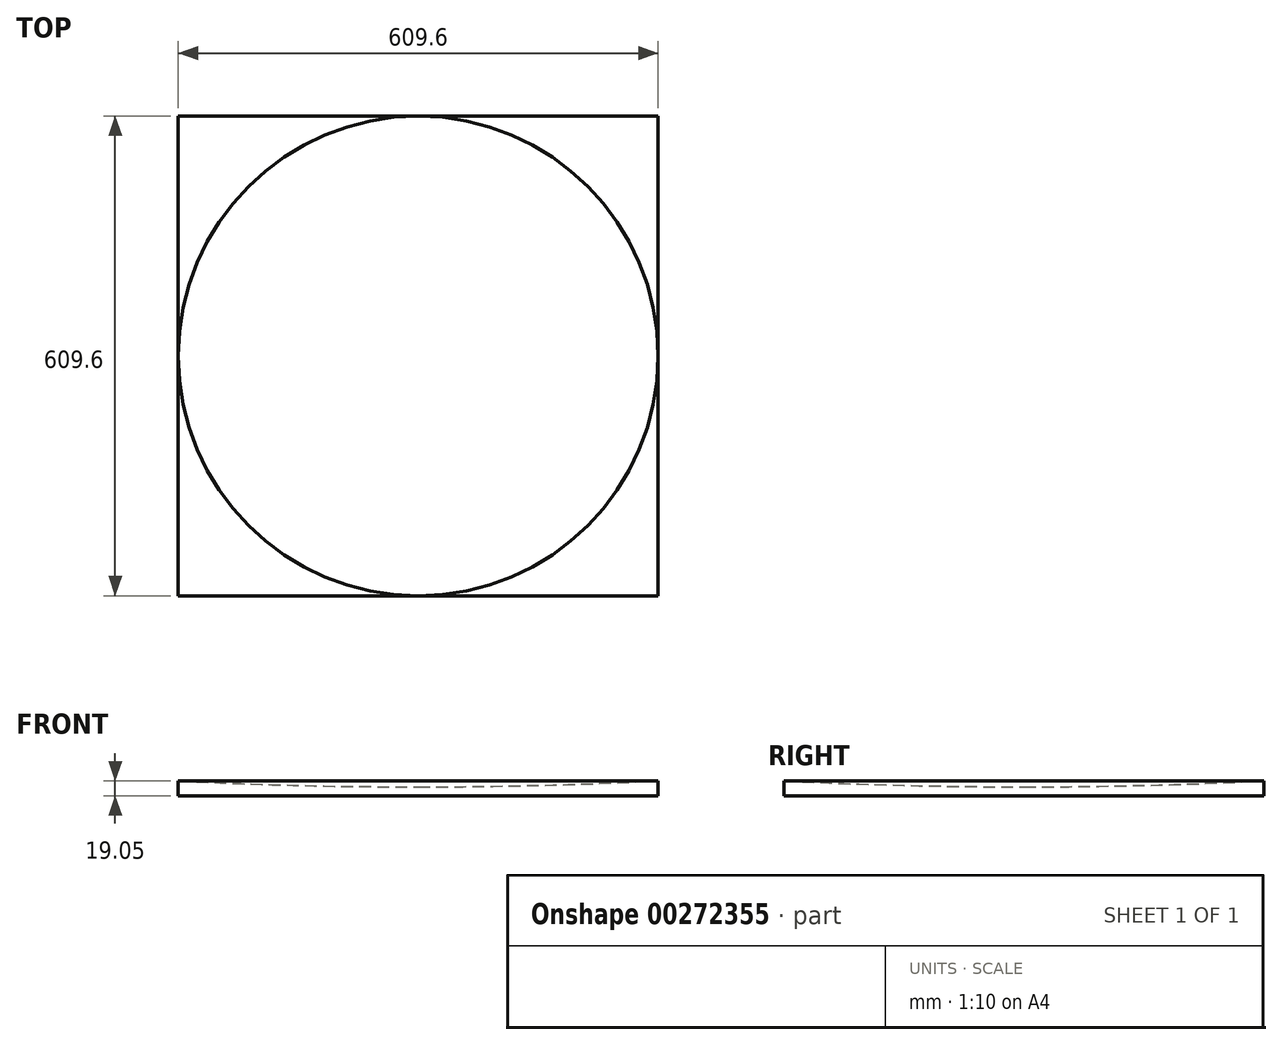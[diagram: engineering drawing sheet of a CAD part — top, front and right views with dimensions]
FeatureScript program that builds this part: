
annotation { "Feature Type Name" : "Feature", "Feature Type Description" : "" }
export const myFeature = defineFeature(function(context is Context, id is Id, definition is map)
    precondition{}
    {
        {
            var Q0;
            Q0=qCreatedBy(makeId("Top.planeOp"),FACE);
            var sketch = newSketch(context, id + "F0", { "sketchPlane" : qUnion([Q0])});
            skLineSegment(sketch, "E0.bottom", {"start": v(304.8, 304.8) * mm, "end": v(-304.8, 304.8) * mm});
            skLineSegment(sketch, "E0.top", {"start": v(304.8, -304.8) * mm, "end": v(-304.8, -304.8) * mm});
            skLineSegment(sketch, "E0.left", {"start": v(304.8, 304.8) * mm, "end": v(304.8, -304.8) * mm});
            skLineSegment(sketch, "E0.right", {"start": v(-304.8, 304.8) * mm, "end": v(-304.8, -304.8) * mm});
            skPoint(sketch, "E0.middle", {"position": v(0, 0) * mm});
            skSolve(sketch);
        }
        {
            var Q0;
            Q0=makeQuery(id+"F0.imprint","IMPRINT",FACE,{"disambiguationData":[TD([[makeQuery(id+"F0.imprint","IMPRINT",EDGE,{"derivedFrom":sQuery(id+"F0.wireOp",EDGE,"E0.bottom")}),1.0]])]});
            extrude(context, id + "F1", {"entities" : qUnion([Q0]), "depth" : 19.05 * mm});
        }
        {
            var Q0;
            Q0=qCreatedBy(makeId("Front.planeOp"),FACE);
            var sketch = newSketch(context, id + "F2", { "sketchPlane" : qUnion([Q0])});
            skArc(sketch, "E1", {"start": v(0, 11.43) * mm, "mid": v(4310.52, 1796.9) * mm, "end": v(6096, 6107.43) * mm});
            skLineSegment(sketch, "E2", {"start": v(-8593.09, 6107.43) * mm, "end": v(10366.9, 6107.43) * mm, "construction": true});
            skLineSegment(sketch, "E3", {"start": v(0, 6107.43) * mm, "end": v(0, -693.63) * mm});
            skLineSegment(sketch, "E4", {"start": v(6096, 6107.43) * mm, "end": v(0, 6107.43) * mm});
            skSolve(sketch);
        }
        {
            var Q0;
            {var subQ0=sQuery(id+"F2.wireOp",EDGE,"E1");Q0=makeQuery(id+"F2.imprint","IMPRINT",FACE,{"disambiguationData":[TD([[makeQuery(id+"F2.imprint","IMPRINT",EDGE,{"derivedFrom":subQ0}),1.0]])]});}
            var Q1;
            Q1=sQuery(id+"F2.wireOp",EDGE,"E3");
            revolve(context, id + "F3", {"operationType" : NewBodyOperationType.REMOVE, "entities" : qUnion([Q0]), "axis" : qUnion([Q1]), "revolveType" : RevolveType.FULL, "oppositeDirection" : true});
        }
    });
